FCSTD DOCUMENT  (FreeCAD 1.1R39747 (Git))
Label: FieldAssembly
License: All rights reserved
LicenseURL: https://en.wikipedia.org/wiki/All_rights_reserved
objects: App::Link×43, App::FeaturePython×43, App::Point×2, Assembly::JointGroup×2, Assembly::AssemblyLink×1, Assembly::AssemblyObject×1
EXTERNAL_REF file=RobotAssembly.FCStd obj=Assembly
EXTERNAL_REF file=RobotAssembly.FCStd obj=Body
EXTERNAL_REF file=RobotAssembly.FCStd obj=am_3637_NeveRest_Orbital_20_Gearmotor_REV2
EXTERNAL_REF file=RobotAssembly.FCStd obj=Motor_Mount_Right
EXTERNAL_REF file=RobotAssembly.FCStd obj=Motor_Mount_Left
EXTERNAL_REF file=RobotAssembly.FCStd obj=Link
EXTERNAL_REF file=RobotAssembly.FCStd obj=Slides_Mount
EXTERNAL_REF file=RobotAssembly.FCStd obj=Screw
EXTERNAL_REF file=RobotAssembly.FCStd obj=Screw001
EXTERNAL_REF file=RobotAssembly.FCStd obj=Screw002
EXTERNAL_REF file=RobotAssembly.FCStd obj=Screw003
EXTERNAL_REF file=RobotAssembly.FCStd obj=Screw004
EXTERNAL_REF file=RobotAssembly.FCStd obj=Screw005
EXTERNAL_REF file=RobotAssembly.FCStd obj=Screw006
EXTERNAL_REF file=RobotAssembly.FCStd obj=Screw007
EXTERNAL_REF file=RobotAssembly.FCStd obj=Link001
EXTERNAL_REF file=RobotAssembly.FCStd obj=Ras_Pi_3B_179
EXTERNAL_REF file=RobotAssembly.FCStd obj=Link002
EXTERNAL_REF file=RobotAssembly.FCStd obj=Screw008
EXTERNAL_REF file=RobotAssembly.FCStd obj=Link003
EXTERNAL_REF file=RobotAssembly.FCStd obj=Nut
EXTERNAL_REF file=RobotAssembly.FCStd obj=Body_Top
EXTERNAL_REF file=RobotAssembly.FCStd obj=Nut001
EXTERNAL_REF file=RobotAssembly.FCStd obj=Link004
EXTERNAL_REF file=RobotAssembly.FCStd obj=Link005
EXTERNAL_REF file=RobotAssembly.FCStd obj=Link007
EXTERNAL_REF file=RobotAssembly.FCStd obj=Link008
EXTERNAL_REF file=RobotAssembly.FCStd obj=Link009
EXTERNAL_REF file=RobotAssembly.FCStd obj=Link010
EXTERNAL_REF file=RobotAssembly.FCStd obj=Link011
EXTERNAL_REF file=RobotAssembly.FCStd obj=Link013
EXTERNAL_REF file=RobotAssembly.FCStd obj=Link012
EXTERNAL_REF file=RobotAssembly.FCStd obj=Link014
EXTERNAL_REF file=RobotAssembly.FCStd obj=Link015
EXTERNAL_REF file=RobotAssembly.FCStd obj=Link016
EXTERNAL_REF file=RobotAssembly.FCStd obj=Link017
EXTERNAL_REF file=RobotAssembly.FCStd obj=Link018
EXTERNAL_REF file=RobotAssembly.FCStd obj=SAR2_20_b
EXTERNAL_REF file=RobotAssembly.FCStd obj=SAR2_20_r
EXTERNAL_REF file=RobotAssembly.FCStd obj=_609_0613_0007
EXTERNAL_REF file=RobotAssembly.FCStd obj=StringGuard
EXTERNAL_REF file=RobotAssembly.FCStd obj=Screw009
EXTERNAL_REF file=RobotAssembly.FCStd obj=Link019
EXTERNAL_REF file=Field/Field.FCStd obj=Body

FEATURE [App::Point] Origin001
  Role = Origin
FEATURE [App::Point] Origin003
  Role = Origin
FEATURE [App::Link] Body
  LinkPlacement = pos=(-0.033439,2.054e-13,75.5) rot=(0,0,1;0rad)
  LinkedObject = -> <external RobotAssembly.FCStd>#Body
  Placement = pos=(-0.033439,2.054e-13,75.5) rot=(0,0,1;0rad)
FEATURE [App::Link] am_3637_NeveRest_Orbital_20_Gearmotor_REV2  label="am-3637 NeveRest Orbital 20 Gearmotor REV2"
  LinkPlacement = pos=(0.810701,-20.1819,58.942) rot=(1,0,0;1.5708rad)
  LinkedObject = -> <external RobotAssembly.FCStd>#am_3637_NeveRest_Orbital_20_Gearmotor_REV2
  Placement = pos=(0.810701,-20.1819,58.942) rot=(1,0,0;1.5708rad)
FEATURE [App::Link] Motor_Mount_Right  label="Motor Mount Right"
  LinkPlacement = pos=(-0.033439,2.089e-13,75.5) rot=(0,0,1;0rad)
  LinkedObject = -> <external RobotAssembly.FCStd>#Motor_Mount_Right
  Placement = pos=(-0.033439,2.089e-13,75.5) rot=(0,0,1;0rad)
FEATURE [App::Link] Motor_Mount_Left  label="Motor Mount Left"
  LinkPlacement = pos=(-85.0334,105,75.5) rot=(0,0,1;0rad)
  LinkedObject = -> <external RobotAssembly.FCStd>#Motor_Mount_Left
  Placement = pos=(-85.0334,105,75.5) rot=(0,0,1;0rad)
FEATURE [App::Link] Link  label="am-3637 NeveRest Orbital 20 Gearmotor REV003"
  LinkPlacement = pos=(-0.877579,20.1819,58.942) rot=(0,0.707107,0.707107;3.14159rad)
  LinkedObject = -> <external RobotAssembly.FCStd>#Link
  Placement = pos=(-0.877579,20.1819,58.942) rot=(0,0.707107,0.707107;3.14159rad)
FEATURE [App::Link] Slides_Mount  label="Slides Mount"
  LinkPlacement = pos=(-0.033439,1.861e-13,75.5) rot=(0,0,1;0rad)
  LinkedObject = -> <external RobotAssembly.FCStd>#Slides_Mount
  Placement = pos=(-0.033439,1.861e-13,75.5) rot=(0,0,1;0rad)
FEATURE [App::Link] Screw  label="M4x16-Screw053"
  LinkPlacement = pos=(79.9666,-25,105.5) rot=(0.57735,0.57735,0.57735;2.0944rad)
  LinkedObject = -> <external RobotAssembly.FCStd>#Screw
  Placement = pos=(79.9666,-25,105.5) rot=(0.57735,0.57735,0.57735;2.0944rad)
FEATURE [App::Link] Screw001  label="M4x16-Screw"
  LinkPlacement = pos=(79.9666,25,105.5) rot=(0.57735,0.57735,0.57735;2.0944rad)
  LinkedObject = -> <external RobotAssembly.FCStd>#Screw001
  Placement = pos=(79.9666,25,105.5) rot=(0.57735,0.57735,0.57735;2.0944rad)
FEATURE [App::Link] Screw002  label="M4x16-Screw054"
  LinkPlacement = pos=(79.9666,-25,80.5) rot=(0.57735,0.57735,0.57735;2.0944rad)
  LinkedObject = -> <external RobotAssembly.FCStd>#Screw002
  Placement = pos=(79.9666,-25,80.5) rot=(0.57735,0.57735,0.57735;2.0944rad)
FEATURE [App::Link] Screw003  label="M4x16-Screw055"
  LinkPlacement = pos=(79.9666,25,80.5) rot=(0.57735,0.57735,0.57735;2.0944rad)
  LinkedObject = -> <external RobotAssembly.FCStd>#Screw003
  Placement = pos=(79.9666,25,80.5) rot=(0.57735,0.57735,0.57735;2.0944rad)
FEATURE [App::Link] Screw004  label="M4x16-Screw056"
  LinkPlacement = pos=(-37.5334,-55,99.25) rot=(1,0,0;1.5708rad)
  LinkedObject = -> <external RobotAssembly.FCStd>#Screw004
  Placement = pos=(-37.5334,-55,99.25) rot=(1,0,0;1.5708rad)
FEATURE [App::Link] Screw005  label="M4x16-Screw057"
  LinkPlacement = pos=(-0.033439,-55,89.25) rot=(1,0,0;1.5708rad)
  LinkedObject = -> <external RobotAssembly.FCStd>#Screw005
  Placement = pos=(-0.033439,-55,89.25) rot=(1,0,0;1.5708rad)
FEATURE [App::Link] Screw006  label="M4x16-Screw058"
  LinkPlacement = pos=(-37.5334,-55,79.25) rot=(1,0,0;1.5708rad)
  LinkedObject = -> <external RobotAssembly.FCStd>#Screw006
  Placement = pos=(-37.5334,-55,79.25) rot=(1,0,0;1.5708rad)
FEATURE [App::Link] Screw007  label="M4x16-Screw059"
  LinkPlacement = pos=(37.4666,-55,79.25) rot=(1,0,0;1.5708rad)
  LinkedObject = -> <external RobotAssembly.FCStd>#Screw007
  Placement = pos=(37.4666,-55,79.25) rot=(1,0,0;1.5708rad)
FEATURE [App::Link] Link001  label="M4x16-Screw026"
  LinkPlacement = pos=(37.4666,-55,99.25) rot=(1,0,0;1.5708rad)
  LinkedObject = -> <external RobotAssembly.FCStd>#Link001
  Placement = pos=(37.4666,-55,99.25) rot=(1,0,0;1.5708rad)
FEATURE [App::Link] Ras_Pi_3B_179  label="Ras Pi 3B+179"
  LinkPlacement = pos=(19.4666,28,78.5) rot=(0,0.707107,0.707107;3.14159rad)
  LinkedObject = -> <external RobotAssembly.FCStd>#Ras_Pi_3B_179
  Placement = pos=(19.4666,28,78.5) rot=(0,0.707107,0.707107;3.14159rad)
FEATURE [App::Link] Link002  label="M4x14-Screw001"
  LinkPlacement = pos=(82.5201,-6.931e-13,138) rot=(0,1,0;1.5708rad)
  LinkedObject = -> <external RobotAssembly.FCStd>#Link002
  Placement = pos=(82.5201,-6.931e-13,138) rot=(0,1,0;1.5708rad)
FEATURE [App::Link] Screw008  label="M4x14-Screw"
  LinkPlacement = pos=(82.5201,-6.878e-13,223) rot=(0,1,0;1.5708rad)
  LinkedObject = -> <external RobotAssembly.FCStd>#Screw008
  Placement = pos=(82.5201,-6.878e-13,223) rot=(0,1,0;1.5708rad)
FEATURE [App::Link] Link003  label="M4-Nut001"
  LinkPlacement = pos=(71.7666,-6.97e-13,223) rot=(0.57735,0.57735,0.57735;2.0944rad)
  LinkedObject = -> <external RobotAssembly.FCStd>#Link003
  Placement = pos=(71.7666,-6.97e-13,223) rot=(0.57735,0.57735,0.57735;2.0944rad)
FEATURE [App::Link] Nut  label="M4-Nut"
  LinkPlacement = pos=(71.7666,-7.48e-13,138) rot=(0.57735,0.57735,0.57735;2.0944rad)
  LinkedObject = -> <external RobotAssembly.FCStd>#Nut
  Placement = pos=(71.7666,-7.48e-13,138) rot=(0.57735,0.57735,0.57735;2.0944rad)
FEATURE [App::Link] Body_Top  label="Body Top"
  LinkPlacement = pos=(-0.033439,2.036e-13,75.5) rot=(0,0,1;0rad)
  LinkedObject = -> <external RobotAssembly.FCStd>#Body_Top
  Placement = pos=(-0.033439,2.036e-13,75.5) rot=(0,0,1;0rad)
FEATURE [App::Link] Nut001  label="M4-Nut013"
  LinkPlacement = pos=(37.4666,-41.8,99.25) rot=(1,0,0;1.5708rad)
  LinkedObject = -> <external RobotAssembly.FCStd>#Nut001
  Placement = pos=(37.4666,-41.8,99.25) rot=(1,0,0;1.5708rad)
FEATURE [App::Link] Link004  label="M4-Nut003"
  LinkPlacement = pos=(-0.033439,-41.8,89.25) rot=(1,0,0;1.5708rad)
  LinkedObject = -> <external RobotAssembly.FCStd>#Link004
  Placement = pos=(-0.033439,-41.8,89.25) rot=(1,0,0;1.5708rad)
FEATURE [App::Link] Link005  label="M4-Nut004"
  LinkPlacement = pos=(-37.5334,-41.8,79.25) rot=(1,0,0;1.5708rad)
  LinkedObject = -> <external RobotAssembly.FCStd>#Link005
  Placement = pos=(-37.5334,-41.8,79.25) rot=(1,0,0;1.5708rad)
FEATURE [App::Link] Link007  label="M4-Nut006"
  LinkPlacement = pos=(-37.5334,-41.8,99.25) rot=(1,0,0;1.5708rad)
  LinkedObject = -> <external RobotAssembly.FCStd>#Link007
  Placement = pos=(-37.5334,-41.8,99.25) rot=(1,0,0;1.5708rad)
FEATURE [App::Link] Link008  label="M4-Nut007"
  LinkPlacement = pos=(-0.033439,41.8,89.25) rot=(1,0,0;4.71239rad)
  LinkedObject = -> <external RobotAssembly.FCStd>#Link008
  Placement = pos=(-0.033439,41.8,89.25) rot=(1,0,0;4.71239rad)
FEATURE [App::Link] Link009  label="M4-Nut008"
  LinkPlacement = pos=(-37.5334,41.8,99.25) rot=(1,0,0;4.71239rad)
  LinkedObject = -> <external RobotAssembly.FCStd>#Link009
  Placement = pos=(-37.5334,41.8,99.25) rot=(1,0,0;4.71239rad)
FEATURE [App::Link] Link010  label="M4-Nut009"
  LinkPlacement = pos=(-37.5334,41.8,79.25) rot=(1,0,0;4.71239rad)
  LinkedObject = -> <external RobotAssembly.FCStd>#Link010
  Placement = pos=(-37.5334,41.8,79.25) rot=(1,0,0;4.71239rad)
FEATURE [App::Link] Link011  label="M4-Nut010"
  LinkPlacement = pos=(37.4666,41.8,99.25) rot=(1,0,0;4.71239rad)
  LinkedObject = -> <external RobotAssembly.FCStd>#Link011
  Placement = pos=(37.4666,41.8,99.25) rot=(1,0,0;4.71239rad)
FEATURE [App::Link] Link013  label="M4-Nut012"
  LinkPlacement = pos=(37.4666,41.8,79.25) rot=(1,0,0;4.71239rad)
  LinkedObject = -> <external RobotAssembly.FCStd>#Link013
  Placement = pos=(37.4666,41.8,79.25) rot=(1,0,0;4.71239rad)
FEATURE [App::Link] Link012  label="M4-Nut011"
  LinkPlacement = pos=(37.4666,-41.8,79.25) rot=(1,0,0;1.5708rad)
  LinkedObject = -> <external RobotAssembly.FCStd>#Link012
  Placement = pos=(37.4666,-41.8,79.25) rot=(1,0,0;1.5708rad)
FEATURE [App::Link] Link014  label="M4x16-Screw034"
  LinkPlacement = pos=(-37.5334,55,99.25) rot=(0,0.707107,0.707107;3.14159rad)
  LinkedObject = -> <external RobotAssembly.FCStd>#Link014
  Placement = pos=(-37.5334,55,99.25) rot=(0,0.707107,0.707107;3.14159rad)
FEATURE [App::Link] Link015  label="M4x16-Screw035"
  LinkPlacement = pos=(37.4666,55,79.25) rot=(0,0.707107,0.707107;3.14159rad)
  LinkedObject = -> <external RobotAssembly.FCStd>#Link015
  Placement = pos=(37.4666,55,79.25) rot=(0,0.707107,0.707107;3.14159rad)
FEATURE [App::Link] Link016  label="M4x16-Screw036"
  LinkPlacement = pos=(-37.5334,55,79.25) rot=(0,0.707107,0.707107;3.14159rad)
  LinkedObject = -> <external RobotAssembly.FCStd>#Link016
  Placement = pos=(-37.5334,55,79.25) rot=(0,0.707107,0.707107;3.14159rad)
FEATURE [App::Link] Link017  label="M4x16-Screw037"
  LinkPlacement = pos=(37.4666,55,99.25) rot=(0,0.707107,0.707107;3.14159rad)
  LinkedObject = -> <external RobotAssembly.FCStd>#Link017
  Placement = pos=(37.4666,55,99.25) rot=(0,0.707107,0.707107;3.14159rad)
FEATURE [App::Link] Link018  label="M4x16-Screw038"
  LinkPlacement = pos=(-0.033439,55,89.25) rot=(0,0.707107,0.707107;3.14159rad)
  LinkedObject = -> <external RobotAssembly.FCStd>#Link018
  Placement = pos=(-0.033439,55,89.25) rot=(0,0.707107,0.707107;3.14159rad)
FEATURE [App::Link] SAR2_20_b  label="SAR2-20_b"
  LinkPlacement = pos=(87.3666,-10,38) rot=(0,0,1;0rad)
  LinkedObject = -> <external RobotAssembly.FCStd>#SAR2_20_b
  Placement = pos=(87.3666,-10,38) rot=(0,0,1;0rad)
FEATURE [App::Link] SAR2_20_r  label="SAR2-20_r"
  LinkPlacement = pos=(82.1666,-6.05,158) rot=(0,0,1;0rad)
  LinkedObject = -> <external RobotAssembly.FCStd>#SAR2_20_r
  Placement = pos=(82.1666,-6.05,158) rot=(0,0,1;0rad)
FEATURE [App::Link] _609_0613_0007  label="1609-0613-0007"
  LinkPlacement = pos=(64.9666,18.5,220) rot=(0,1,0;1.57081rad)
  LinkedObject = -> <external RobotAssembly.FCStd>#_609_0613_0007
  Placement = pos=(64.9666,18.5,220) rot=(0,1,0;1.57081rad)
FEATURE [App::Link] StringGuard
  LinkPlacement = pos=(64.9666,18.25,220) rot=(0,0,1;0rad)
  LinkedObject = -> <external RobotAssembly.FCStd>#StringGuard
  Placement = pos=(64.9666,18.25,220) rot=(0,0,1;0rad)
FEATURE [App::Link] Screw009  label="M4x25-Screw"
  LinkPlacement = pos=(64.9666,27.5,220) rot=(1,0,0;4.71239rad)
  LinkedObject = -> <external RobotAssembly.FCStd>#Screw009
  Placement = pos=(64.9666,27.5,220) rot=(1,0,0;4.71239rad)
FEATURE [App::Link] Link019  label="M4-Nut014"
  LinkPlacement = pos=(64.9666,10,220) rot=(0,-0.707107,0.707107;3.14159rad)
  LinkedObject = -> <external RobotAssembly.FCStd>#Link019
  Placement = pos=(64.9666,10,220) rot=(0,-0.707107,0.707107;3.14159rad)
FEATURE [App::Link] Field
  LinkedObject = -> <external Field/Field.FCStd>#Body
FEATURE [App::FeaturePython] GroundedJoint  # Assembly grounded joint (typed FeaturePython)
  ObjectToGround = -> Field
FEATURE [App::FeaturePython] Joint  label="Distance"  # Assembly joint (typed FeaturePython)
  Activated = true
  AngleMax = 0
  AngleMin = 0
  Detach1 = false
  Detach2 = false
  Distance = -50
  Distance2 = 0
  EnableAngleMax = false
  EnableAngleMin = false
  EnableLengthMax = false
  EnableLengthMin = false
  JointType = 5 (Distance)
  LengthMax = 0
  LengthMin = 0
  Placement1 = pos=(0.033439,-1.12e-13,-7.5) rot=(0,0,1;0rad)
  Placement2 = pos=(-1.386e-13,1.101e-13,18) rot=(0,0,1;0rad)
  Reference1 = -> Assembly [Robot_Assembly.Body.Face26,Robot_Assembly.Body.Vertex125]
  Reference2 = -> Assembly [Field.Face5,Field.Vertex11]
FEATURE [Assembly::JointGroup] Joints
  Group = -> [GroundedJoint,Joint]
FEATURE [App::FeaturePython] Joint002  label="Fixed"  # Assembly joint (typed FeaturePython)
  Activated = true
  AngleMax = 0
  AngleMin = 0
  Detach1 = false
  Detach2 = false
  Distance = 0
  Distance2 = 0
  EnableAngleMax = false
  EnableAngleMin = false
  EnableLengthMax = false
  EnableLengthMin = false
  JointType = 0 (Fixed)
  LengthMax = 0
  LengthMin = 0
  Placement1 = pos=(0,-50,13.75) rot=(1,0,0;1.5708rad)
  Placement2 = pos=(0,-50,13.75) rot=(1,0,0;1.5708rad)
  Reference1 = -> Assembly [Robot_Assembly.Motor_Mount_Right.Edge47,Robot_Assembly.Motor_Mount_Right.Edge47]
  Reference2 = -> Assembly [Robot_Assembly.Body.Edge30,Robot_Assembly.Body.Edge30]
FEATURE [App::FeaturePython] Joint003  label="Fixed001"  # Assembly joint (typed FeaturePython)
  Activated = true
  AngleMax = 0
  AngleMin = 0
  Detach1 = false
  Detach2 = false
  Distance = 0
  Distance2 = 0
  EnableAngleMax = false
  EnableAngleMin = false
  EnableLengthMax = false
  EnableLengthMin = false
  JointType = 0 (Fixed)
  LengthMax = 0
  LengthMin = 0
  Offset2 = pos=(0,0,0) rot=(0,0,1;3.14159rad)
  Placement1 = pos=(85,-55,13.75) rot=(0,0.707107,0.707107;3.14159rad)
  Placement2 = pos=(0,50,13.75) rot=(0,-0.707107,0.707107;3.14159rad)
  Reference1 = -> Assembly [Robot_Assembly.Motor_Mount_Left.Edge48,Robot_Assembly.Motor_Mount_Left.Edge48]
  Reference2 = -> Assembly [Robot_Assembly.Body.Edge59,Robot_Assembly.Body.Edge59]
FEATURE [App::FeaturePython] Joint004  label="Fixed002"  # Assembly joint (typed FeaturePython)
  Activated = true
  AngleMax = 0
  AngleMin = 0
  Detach1 = false
  Detach2 = false
  Distance = 0
  Distance2 = 0
  EnableAngleMax = false
  EnableAngleMin = false
  EnableLengthMax = false
  EnableLengthMin = false
  JointType = 0 (Fixed)
  LengthMax = 0
  LengthMin = 0
  Placement1 = pos=(0,0,32.1564) rot=(0,0,1;0rad)
  Placement2 = pos=(-28,-50,-29) rot=(1,0,0;1.5708rad)
  Reference1 = -> <external RobotAssembly.FCStd>#Assembly [am_3637_NeveRest_Orbital_20_Gearmotor_REV2.Part__Feature.Edge163,am_3637_NeveRest_Orbital_20_Gearmotor_REV2.Part__Feature.Edge163]
  Reference2 = -> Assembly [Robot_Assembly.Motor_Mount_Right.Edge38,Robot_Assembly.Motor_Mount_Right.Edge38]
FEATURE [App::FeaturePython] Joint005  label="Fixed003"  # Assembly joint (typed FeaturePython)
  Activated = true
  AngleMax = 0
  AngleMin = 0
  Detach1 = false
  Detach2 = false
  Distance = 0
  Distance2 = 0
  EnableAngleMax = false
  EnableAngleMin = false
  EnableLengthMax = false
  EnableLengthMin = false
  JointType = 0 (Fixed)
  LengthMax = 0
  LengthMin = 0
  Placement1 = pos=(0,0,32.1564) rot=(0,0,1;0rad)
  Placement2 = pos=(113,-55,-29) rot=(0,0.707107,0.707107;3.14159rad)
  Reference1 = -> <external RobotAssembly.FCStd>#Assembly [Link.Part__Feature.Edge163,Link.Part__Feature.Edge163]
  Reference2 = -> Assembly [Robot_Assembly.Motor_Mount_Left.Edge39,Robot_Assembly.Motor_Mount_Left.Edge39]
FEATURE [App::FeaturePython] Joint009  label="Fixed005"  # Assembly joint (typed FeaturePython)
  Activated = true
  AngleMax = 0
  AngleMin = 0
  Detach1 = false
  Detach2 = false
  Distance = 0
  Distance2 = 0
  EnableAngleMax = false
  EnableAngleMin = false
  EnableLengthMax = false
  EnableLengthMin = false
  JointType = 0 (Fixed)
  LengthMax = 0
  LengthMin = 0
  Placement1 = pos=(75,25,30) rot=(0.57735,0.57735,0.57735;2.0944rad)
  Placement2 = pos=(75,25,30) rot=(0.57735,0.57735,0.57735;2.0944rad)
  Reference1 = -> Assembly [Robot_Assembly.Slides_Mount.Edge60,Robot_Assembly.Slides_Mount.Edge60]
  Reference2 = -> Assembly [Robot_Assembly.Body.Edge44,Robot_Assembly.Body.Edge44]
FEATURE [App::FeaturePython] Joint012  label="Fixed007"  # Assembly joint (typed FeaturePython)
  Activated = true
  AngleMax = 0
  AngleMin = 0
  Detach1 = false
  Detach2 = false
  Distance = 0
  Distance2 = 0
  EnableAngleMax = false
  EnableAngleMin = false
  EnableLengthMax = false
  EnableLengthMin = false
  JointType = 0 (Fixed)
  LengthMax = 0
  LengthMin = 0
  Placement2 = pos=(80,-25,30) rot=(0.57735,0.57735,0.57735;2.0944rad)
  Reference1 = -> Assembly [Robot_Assembly.Screw.Edge26,Robot_Assembly.Screw.Edge26]
  Reference2 = -> Assembly [Robot_Assembly.Slides_Mount.Edge74,Robot_Assembly.Slides_Mount.Edge74]
FEATURE [App::FeaturePython] Joint013  label="Fixed008"  # Assembly joint (typed FeaturePython)
  Activated = true
  AngleMax = 0
  AngleMin = 0
  Detach1 = false
  Detach2 = false
  Distance = 0
  Distance2 = 0
  EnableAngleMax = false
  EnableAngleMin = false
  EnableLengthMax = false
  EnableLengthMin = false
  JointType = 0 (Fixed)
  LengthMax = 0
  LengthMin = 0
  Placement2 = pos=(80,-25,5) rot=(0.57735,0.57735,0.57735;2.0944rad)
  Reference1 = -> Assembly [Robot_Assembly.Screw002.Edge26,Robot_Assembly.Screw002.Edge26]
  Reference2 = -> Assembly [Robot_Assembly.Slides_Mount.Edge72,Robot_Assembly.Slides_Mount.Edge72]
FEATURE [App::FeaturePython] Joint014  label="Fixed009"  # Assembly joint (typed FeaturePython)
  Activated = true
  AngleMax = 0
  AngleMin = 0
  Detach1 = false
  Detach2 = false
  Distance = 0
  Distance2 = 0
  EnableAngleMax = false
  EnableAngleMin = false
  EnableLengthMax = false
  EnableLengthMin = false
  JointType = 0 (Fixed)
  LengthMax = 0
  LengthMin = 0
  Placement2 = pos=(80,25,30) rot=(0.57735,0.57735,0.57735;2.0944rad)
  Reference1 = -> Assembly [Robot_Assembly.Screw001.Edge26,Robot_Assembly.Screw001.Edge26]
  Reference2 = -> Assembly [Robot_Assembly.Slides_Mount.Edge70,Robot_Assembly.Slides_Mount.Edge70]
FEATURE [App::FeaturePython] Joint015  label="Fixed010"  # Assembly joint (typed FeaturePython)
  Activated = true
  AngleMax = 0
  AngleMin = 0
  Detach1 = false
  Detach2 = false
  Distance = 0
  Distance2 = 0
  EnableAngleMax = false
  EnableAngleMin = false
  EnableLengthMax = false
  EnableLengthMin = false
  JointType = 0 (Fixed)
  LengthMax = 0
  LengthMin = 0
  Placement2 = pos=(80,25,5) rot=(0.57735,0.57735,0.57735;2.0944rad)
  Reference1 = -> Assembly [Robot_Assembly.Screw003.Edge26,Robot_Assembly.Screw003.Edge26]
  Reference2 = -> Assembly [Robot_Assembly.Slides_Mount.Edge68,Robot_Assembly.Slides_Mount.Edge68]
FEATURE [App::FeaturePython] Joint016  label="Fixed011"  # Assembly joint (typed FeaturePython)
  Activated = true
  AngleMax = 0
  AngleMin = 0
  Detach1 = false
  Detach2 = false
  Distance = 0
  Distance2 = 0
  EnableAngleMax = false
  EnableAngleMin = false
  EnableLengthMax = false
  EnableLengthMin = false
  JointType = 0 (Fixed)
  LengthMax = 0
  LengthMin = 0
  Placement2 = pos=(-37.5,-55,23.75) rot=(1,0,0;1.5708rad)
  Reference1 = -> Assembly [Robot_Assembly.Screw004.Edge26,Robot_Assembly.Screw004.Edge26]
  Reference2 = -> Assembly [Robot_Assembly.Motor_Mount_Right.Edge45,Robot_Assembly.Motor_Mount_Right.Edge45]
FEATURE [App::FeaturePython] Joint017  label="Fixed012"  # Assembly joint (typed FeaturePython)
  Activated = true
  AngleMax = 0
  AngleMin = 0
  Detach1 = false
  Detach2 = false
  Distance = 0
  Distance2 = 0
  EnableAngleMax = false
  EnableAngleMin = false
  EnableLengthMax = false
  EnableLengthMin = false
  JointType = 0 (Fixed)
  LengthMax = 0
  LengthMin = 0
  Placement2 = pos=(-37.5,-55,3.75) rot=(1,0,0;1.5708rad)
  Reference1 = -> Assembly [Robot_Assembly.Screw006.Edge26,Robot_Assembly.Screw006.Edge26]
  Reference2 = -> Assembly [Robot_Assembly.Motor_Mount_Right.Edge54,Robot_Assembly.Motor_Mount_Right.Edge54]
FEATURE [App::FeaturePython] Joint018  label="Fixed013"  # Assembly joint (typed FeaturePython)
  Activated = true
  AngleMax = 0
  AngleMin = 0
  Detach1 = false
  Detach2 = false
  Distance = 0
  Distance2 = 0
  EnableAngleMax = false
  EnableAngleMin = false
  EnableLengthMax = false
  EnableLengthMin = false
  JointType = 0 (Fixed)
  LengthMax = 0
  LengthMin = 0
  Placement2 = pos=(0,-55,13.75) rot=(1,0,0;1.5708rad)
  Reference1 = -> Assembly [Robot_Assembly.Screw005.Edge26,Robot_Assembly.Screw005.Edge26]
  Reference2 = -> Assembly [Robot_Assembly.Motor_Mount_Right.Edge48,Robot_Assembly.Motor_Mount_Right.Edge48]
FEATURE [App::FeaturePython] Joint019  label="Fixed014"  # Assembly joint (typed FeaturePython)
  Activated = true
  AngleMax = 0
  AngleMin = 0
  Detach1 = false
  Detach2 = false
  Distance = 0
  Distance2 = 0
  EnableAngleMax = false
  EnableAngleMin = false
  EnableLengthMax = false
  EnableLengthMin = false
  JointType = 0 (Fixed)
  LengthMax = 0
  LengthMin = 0
  Placement2 = pos=(37.5,-55,3.75) rot=(1,0,0;1.5708rad)
  Reference1 = -> Assembly [Robot_Assembly.Screw007.Edge26,Robot_Assembly.Screw007.Edge26]
  Reference2 = -> Assembly [Robot_Assembly.Motor_Mount_Right.Edge51,Robot_Assembly.Motor_Mount_Right.Edge51]
FEATURE [App::FeaturePython] Joint020  label="Fixed015"  # Assembly joint (typed FeaturePython)
  Activated = true
  AngleMax = 0
  AngleMin = 0
  Detach1 = false
  Detach2 = false
  Distance = 0
  Distance2 = 0
  EnableAngleMax = false
  EnableAngleMin = false
  EnableLengthMax = false
  EnableLengthMin = false
  JointType = 0 (Fixed)
  LengthMax = 0
  LengthMin = 0
  Placement2 = pos=(37.5,-55,23.75) rot=(1,0,0;1.5708rad)
  Reference1 = -> Assembly [Robot_Assembly.Link001.Edge26,Robot_Assembly.Link001.Edge26]
  Reference2 = -> Assembly [Robot_Assembly.Motor_Mount_Right.Edge42,Robot_Assembly.Motor_Mount_Right.Edge42]
FEATURE [App::FeaturePython] Joint023  label="Fixed017"  # Assembly joint (typed FeaturePython)
  Activated = true
  AngleMax = 0
  AngleMin = 0
  Detach1 = false
  Detach2 = false
  Distance = 0
  Distance2 = 0
  EnableAngleMax = false
  EnableAngleMin = false
  EnableLengthMax = false
  EnableLengthMin = false
  JointType = 0 (Fixed)
  LengthMax = 0
  LengthMin = 0
  Placement1 = pos=(0,0,3.2) rot=(0,0,1;0rad)
  Placement2 = pos=(75,-1.0119e-12,62.5) rot=(0.57735,0.57735,0.57735;2.0944rad)
  Reference1 = -> Assembly [Robot_Assembly.Nut.Edge2,Robot_Assembly.Nut.Edge2]
  Reference2 = -> Assembly [Robot_Assembly.Slides_Mount.Edge58,Robot_Assembly.Slides_Mount.Edge58]
FEATURE [App::FeaturePython] Joint024  label="Fixed018"  # Assembly joint (typed FeaturePython)
  Activated = true
  AngleMax = 0
  AngleMin = 0
  Detach1 = false
  Detach2 = false
  Distance = 0
  Distance2 = 0
  EnableAngleMax = false
  EnableAngleMin = false
  EnableLengthMax = false
  EnableLengthMin = false
  JointType = 0 (Fixed)
  LengthMax = 0
  LengthMin = 0
  Placement1 = pos=(0,0,3.2) rot=(0,0,1;0rad)
  Placement2 = pos=(75,-9.797e-13,147.5) rot=(0.57735,0.57735,0.57735;2.0944rad)
  Reference1 = -> Assembly [Robot_Assembly.Link003.Edge2,Robot_Assembly.Link003.Edge2]
  Reference2 = -> Assembly [Robot_Assembly.Slides_Mount.Edge57,Robot_Assembly.Slides_Mount.Edge57]
FEATURE [App::FeaturePython] Joint027  label="Fixed021"  # Assembly joint (typed FeaturePython)
  Activated = true
  AngleMax = 0
  AngleMin = 0
  Detach1 = false
  Detach2 = false
  Distance = 0
  Distance2 = 0
  EnableAngleMax = false
  EnableAngleMin = false
  EnableLengthMax = false
  EnableLengthMin = false
  JointType = 0 (Fixed)
  LengthMax = 0
  LengthMin = 0
  Offset2 = pos=(0,0,0) rot=(0,0,1;1.5708rad)
  Placement1 = pos=(-42,-24.5,3) rot=(0,0,1;0rad)
  Placement2 = pos=(61.5,0,-52.5) rot=(0,0.707107,0.707107;3.14159rad)
  Reference1 = -> Assembly [Robot_Assembly.Body.Edge196,Robot_Assembly.Body.Edge196]
  Reference2 = -> <external RobotAssembly.FCStd>#Assembly [Ras_Pi_3B_179.Part__Feature014.Edge10,Ras_Pi_3B_179.Part__Feature014.Edge10]
FEATURE [App::FeaturePython] Joint028  label="Fixed022"  # Assembly joint (typed FeaturePython)
  Activated = true
  AngleMax = 0
  AngleMin = 0
  Detach1 = false
  Detach2 = false
  Distance = 0
  Distance2 = 0
  EnableAngleMax = false
  EnableAngleMin = false
  EnableLengthMax = false
  EnableLengthMin = false
  JointType = 0 (Fixed)
  LengthMax = 0
  LengthMin = 0
  Placement1 = pos=(-66,-41,35) rot=(0,0,1;0rad)
  Placement2 = pos=(-66,-41,35) rot=(0,0,1;0rad)
  Reference1 = -> Assembly [Robot_Assembly.Body.Edge24,Robot_Assembly.Body.Edge24]
  Reference2 = -> Assembly [Robot_Assembly.Body_Top.Edge47,Robot_Assembly.Body_Top.Edge47]
FEATURE [App::FeaturePython] Joint029  label="Fixed023"  # Assembly joint (typed FeaturePython)
  Activated = true
  AngleMax = 0
  AngleMin = 0
  Detach1 = false
  Detach2 = false
  Distance = 0
  Distance2 = 0
  EnableAngleMax = false
  EnableAngleMin = false
  EnableLengthMax = false
  EnableLengthMin = false
  JointType = 0 (Fixed)
  LengthMax = 0
  LengthMin = 0
  Placement1 = pos=(-7.1e-15,0,3.2) rot=(0,0,1;0rad)
  Placement2 = pos=(37.5,-45,23.75) rot=(1,0,0;1.5708rad)
  Reference1 = -> Assembly [Robot_Assembly.Nut001.Edge2,Robot_Assembly.Nut001.Edge2]
  Reference2 = -> Assembly [Robot_Assembly.Body.Edge93,Robot_Assembly.Body.Edge93]
FEATURE [App::FeaturePython] Joint030  label="Fixed024"  # Assembly joint (typed FeaturePython)
  Activated = true
  AngleMax = 0
  AngleMin = 0
  Detach1 = false
  Detach2 = false
  Distance = 0
  Distance2 = 0
  EnableAngleMax = false
  EnableAngleMin = false
  EnableLengthMax = false
  EnableLengthMin = false
  JointType = 0 (Fixed)
  LengthMax = 0
  LengthMin = 0
  Placement1 = pos=(0,0,3.2) rot=(0,0,1;0rad)
  Placement2 = pos=(0,-45,13.75) rot=(1,0,0;1.5708rad)
  Reference1 = -> Assembly [Robot_Assembly.Link004.Edge2,Robot_Assembly.Link004.Edge2]
  Reference2 = -> Assembly [Robot_Assembly.Body.Edge102,Robot_Assembly.Body.Edge102]
FEATURE [App::FeaturePython] Joint031  label="Fixed025"  # Assembly joint (typed FeaturePython)
  Activated = true
  AngleMax = 0
  AngleMin = 0
  Detach1 = false
  Detach2 = false
  Distance = 0
  Distance2 = 0
  EnableAngleMax = false
  EnableAngleMin = false
  EnableLengthMax = false
  EnableLengthMin = false
  JointType = 0 (Fixed)
  LengthMax = 0
  LengthMin = 0
  Placement1 = pos=(-7.1e-15,0,3.2) rot=(0,0,1;0rad)
  Placement2 = pos=(-37.5,-45,23.75) rot=(1,0,0;1.5708rad)
  Reference1 = -> Assembly [Robot_Assembly.Link007.Edge2,Robot_Assembly.Link007.Edge2]
  Reference2 = -> Assembly [Robot_Assembly.Body.Edge92,Robot_Assembly.Body.Edge92]
FEATURE [App::FeaturePython] Joint032  label="Fixed026"  # Assembly joint (typed FeaturePython)
  Activated = true
  AngleMax = 0
  AngleMin = 0
  Detach1 = false
  Detach2 = false
  Distance = 0
  Distance2 = 0
  EnableAngleMax = false
  EnableAngleMin = false
  EnableLengthMax = false
  EnableLengthMin = false
  JointType = 0 (Fixed)
  LengthMax = 0
  LengthMin = 0
  Placement1 = pos=(-7.1e-15,0,3.2) rot=(0,0,1;0rad)
  Placement2 = pos=(-37.5,-45,3.75) rot=(1,0,0;1.5708rad)
  Reference1 = -> Assembly [Robot_Assembly.Link005.Edge2,Robot_Assembly.Link005.Edge2]
  Reference2 = -> Assembly [Robot_Assembly.Body.Edge103,Robot_Assembly.Body.Edge103]
FEATURE [App::FeaturePython] Joint033  label="Fixed027"  # Assembly joint (typed FeaturePython)
  Activated = true
  AngleMax = 0
  AngleMin = 0
  Detach1 = false
  Detach2 = false
  Distance = 0
  Distance2 = 0
  EnableAngleMax = false
  EnableAngleMin = false
  EnableLengthMax = false
  EnableLengthMin = false
  JointType = 0 (Fixed)
  LengthMax = 0
  LengthMin = 0
  Placement1 = pos=(0,0,3.2) rot=(0,0,1;0rad)
  Placement2 = pos=(0,45,13.75) rot=(1,0,0;1.5708rad)
  Reference1 = -> Assembly [Robot_Assembly.Link008.Edge2,Robot_Assembly.Link008.Edge2]
  Reference2 = -> Assembly [Robot_Assembly.Body.Edge135,Robot_Assembly.Body.Edge135]
FEATURE [App::FeaturePython] Joint034  label="Fixed028"  # Assembly joint (typed FeaturePython)
  Activated = true
  AngleMax = 0
  AngleMin = 0
  Detach1 = false
  Detach2 = false
  Distance = 0
  Distance2 = 0
  EnableAngleMax = false
  EnableAngleMin = false
  EnableLengthMax = false
  EnableLengthMin = false
  JointType = 0 (Fixed)
  LengthMax = 0
  LengthMin = 0
  Placement1 = pos=(7.1e-15,0,3.2) rot=(0,0,1;0rad)
  Placement2 = pos=(-37.5,45,23.75) rot=(1,0,0;1.5708rad)
  Reference1 = -> Assembly [Robot_Assembly.Link009.Edge2,Robot_Assembly.Link009.Edge2]
  Reference2 = -> Assembly [Robot_Assembly.Body.Edge126,Robot_Assembly.Body.Edge126]
FEATURE [App::FeaturePython] Joint035  label="Fixed029"  # Assembly joint (typed FeaturePython)
  Activated = true
  AngleMax = 0
  AngleMin = 0
  Detach1 = false
  Detach2 = false
  Distance = 0
  Distance2 = 0
  EnableAngleMax = false
  EnableAngleMin = false
  EnableLengthMax = false
  EnableLengthMin = false
  JointType = 0 (Fixed)
  LengthMax = 0
  LengthMin = 0
  Placement1 = pos=(7.1e-15,0,3.2) rot=(0,0,1;0rad)
  Placement2 = pos=(-37.5,45,3.75) rot=(1,0,0;1.5708rad)
  Reference1 = -> Assembly [Robot_Assembly.Link010.Edge2,Robot_Assembly.Link010.Edge2]
  Reference2 = -> Assembly [Robot_Assembly.Body.Edge137,Robot_Assembly.Body.Edge137]
FEATURE [App::FeaturePython] Joint036  label="Fixed030"  # Assembly joint (typed FeaturePython)
  Activated = true
  AngleMax = 0
  AngleMin = 0
  Detach1 = false
  Detach2 = false
  Distance = 0
  Distance2 = 0
  EnableAngleMax = false
  EnableAngleMin = false
  EnableLengthMax = false
  EnableLengthMin = false
  JointType = 0 (Fixed)
  LengthMax = 0
  LengthMin = 0
  Placement1 = pos=(7.1e-15,0,3.2) rot=(0,0,1;0rad)
  Placement2 = pos=(37.5,45,3.75) rot=(1,0,0;1.5708rad)
  Reference1 = -> Assembly [Robot_Assembly.Link013.Edge2,Robot_Assembly.Link013.Edge2]
  Reference2 = -> Assembly [Robot_Assembly.Body.Edge136,Robot_Assembly.Body.Edge136]
FEATURE [App::FeaturePython] Joint037  label="Fixed031"  # Assembly joint (typed FeaturePython)
  Activated = true
  AngleMax = 0
  AngleMin = 0
  Detach1 = false
  Detach2 = false
  Distance = 0
  Distance2 = 0
  EnableAngleMax = false
  EnableAngleMin = false
  EnableLengthMax = false
  EnableLengthMin = false
  JointType = 0 (Fixed)
  LengthMax = 0
  LengthMin = 0
  Placement1 = pos=(7.1e-15,0,3.2) rot=(0,0,1;0rad)
  Placement2 = pos=(37.5,45,23.75) rot=(1,0,0;1.5708rad)
  Reference1 = -> Assembly [Robot_Assembly.Link011.Edge2,Robot_Assembly.Link011.Edge2]
  Reference2 = -> Assembly [Robot_Assembly.Body.Edge125,Robot_Assembly.Body.Edge125]
FEATURE [App::FeaturePython] Joint038  label="Fixed032"  # Assembly joint (typed FeaturePython)
  Activated = true
  AngleMax = 0
  AngleMin = 0
  Detach1 = false
  Detach2 = false
  Distance = 0
  Distance2 = 0
  EnableAngleMax = false
  EnableAngleMin = false
  EnableLengthMax = false
  EnableLengthMin = false
  JointType = 0 (Fixed)
  LengthMax = 0
  LengthMin = 0
  Placement1 = pos=(-7.1e-15,0,3.2) rot=(0,0,1;0rad)
  Placement2 = pos=(37.5,-45,3.75) rot=(1,0,0;1.5708rad)
  Reference1 = -> Assembly [Robot_Assembly.Link012.Edge2,Robot_Assembly.Link012.Edge2]
  Reference2 = -> Assembly [Robot_Assembly.Body.Edge104,Robot_Assembly.Body.Edge104]
FEATURE [App::FeaturePython] Joint039  label="Fixed033"  # Assembly joint (typed FeaturePython)
  Activated = true
  AngleMax = 0
  AngleMin = 0
  Detach1 = false
  Detach2 = false
  Distance = 0
  Distance2 = 0
  EnableAngleMax = false
  EnableAngleMin = false
  EnableLengthMax = false
  EnableLengthMin = false
  JointType = 0 (Fixed)
  LengthMax = 0
  LengthMin = 0
  Placement2 = pos=(47.5,-50,23.75) rot=(0,0.707107,0.707107;3.14159rad)
  Reference1 = -> Assembly [Robot_Assembly.Link014.Edge26,Robot_Assembly.Link014.Edge26]
  Reference2 = -> Assembly [Robot_Assembly.Motor_Mount_Left.Edge41,Robot_Assembly.Motor_Mount_Left.Edge41]
FEATURE [App::FeaturePython] Joint040  label="Fixed034"  # Assembly joint (typed FeaturePython)
  Activated = true
  AngleMax = 0
  AngleMin = 0
  Detach1 = false
  Detach2 = false
  Distance = 0
  Distance2 = 0
  EnableAngleMax = false
  EnableAngleMin = false
  EnableLengthMax = false
  EnableLengthMin = false
  JointType = 0 (Fixed)
  LengthMax = 0
  LengthMin = 0
  Placement2 = pos=(122.5,-50,3.75) rot=(0,0.707107,0.707107;3.14159rad)
  Reference1 = -> Assembly [Robot_Assembly.Link015.Edge26,Robot_Assembly.Link015.Edge26]
  Reference2 = -> Assembly [Robot_Assembly.Motor_Mount_Left.Edge53,Robot_Assembly.Motor_Mount_Left.Edge53]
FEATURE [App::FeaturePython] Joint041  label="Fixed035"  # Assembly joint (typed FeaturePython)
  Activated = true
  AngleMax = 0
  AngleMin = 0
  Detach1 = false
  Detach2 = false
  Distance = 0
  Distance2 = 0
  EnableAngleMax = false
  EnableAngleMin = false
  EnableLengthMax = false
  EnableLengthMin = false
  JointType = 0 (Fixed)
  LengthMax = 0
  LengthMin = 0
  Placement2 = pos=(85,-50,13.75) rot=(0,0.707107,0.707107;3.14159rad)
  Reference1 = -> Assembly [Robot_Assembly.Link018.Edge26,Robot_Assembly.Link018.Edge26]
  Reference2 = -> Assembly [Robot_Assembly.Motor_Mount_Left.Edge47,Robot_Assembly.Motor_Mount_Left.Edge47]
FEATURE [App::FeaturePython] Joint042  label="Fixed036"  # Assembly joint (typed FeaturePython)
  Activated = true
  AngleMax = 0
  AngleMin = 0
  Detach1 = false
  Detach2 = false
  Distance = 0
  Distance2 = 0
  EnableAngleMax = false
  EnableAngleMin = false
  EnableLengthMax = false
  EnableLengthMin = false
  JointType = 0 (Fixed)
  LengthMax = 0
  LengthMin = 0
  Placement2 = pos=(47.5,-50,3.75) rot=(0,0.707107,0.707107;3.14159rad)
  Reference1 = -> Assembly [Robot_Assembly.Link016.Edge26,Robot_Assembly.Link016.Edge26]
  Reference2 = -> Assembly [Robot_Assembly.Motor_Mount_Left.Edge50,Robot_Assembly.Motor_Mount_Left.Edge50]
FEATURE [App::FeaturePython] Joint043  label="Fixed037"  # Assembly joint (typed FeaturePython)
  Activated = true
  AngleMax = 0
  AngleMin = 0
  Detach1 = false
  Detach2 = false
  Distance = 0
  Distance2 = 0
  EnableAngleMax = false
  EnableAngleMin = false
  EnableLengthMax = false
  EnableLengthMin = false
  JointType = 0 (Fixed)
  LengthMax = 0
  LengthMin = 0
  Placement2 = pos=(122.5,-50,23.75) rot=(0,0.707107,0.707107;3.14159rad)
  Reference1 = -> Assembly [Robot_Assembly.Link017.Edge26,Robot_Assembly.Link017.Edge26]
  Reference2 = -> Assembly [Robot_Assembly.Motor_Mount_Left.Edge44,Robot_Assembly.Motor_Mount_Left.Edge44]
FEATURE [App::FeaturePython] Joint044  label="Slider"  # Assembly joint (typed FeaturePython)
  Activated = true
  AngleMax = 0
  AngleMin = 0
  Detach1 = false
  Detach2 = false
  Distance = 0
  Distance2 = 0
  EnableAngleMax = false
  EnableAngleMin = false
  EnableLengthMax = true
  EnableLengthMin = true
  JointType = 3 (Slider)
  LengthMax = 0
  LengthMin = -120
  Offset1 = pos=(-2.9952,0,0) rot=(0,0,1;0rad)
  Placement1 = pos=(0.302211,6.05,200) rot=(0,0,1;0rad)
  Placement2 = pos=(-4.89776,10,200) rot=(0,0,1;0rad)
  Reference1 = -> Assembly [Robot_Assembly.SAR2_20_r.Face24,Robot_Assembly.SAR2_20_r.Face24]
  Reference2 = -> Assembly [Robot_Assembly.SAR2_20_b.Face57,Robot_Assembly.SAR2_20_b.Face57]
FEATURE [App::FeaturePython] Joint045  label="Fixed038"  # Assembly joint (typed FeaturePython)
  Activated = true
  AngleMax = 0
  AngleMin = 0
  Detach1 = false
  Detach2 = false
  Distance = 0
  Distance2 = 0
  EnableAngleMax = false
  EnableAngleMin = false
  EnableLengthMax = false
  EnableLengthMin = false
  JointType = 0 (Fixed)
  LengthMax = 0
  LengthMin = 0
  Offset2 = pos=(0,0,0) rot=(0,0,-1;1.5708rad)
  Placement1 = pos=(-7.4,10,185) rot=(0,1,0;1.5708rad)
  Placement2 = pos=(80,-9.797e-13,147.5) rot=(0,1,0;1.5708rad)
  Reference1 = -> Assembly [Robot_Assembly.SAR2_20_b.Edge129,Robot_Assembly.SAR2_20_b.Edge129]
  Reference2 = -> Assembly [Robot_Assembly.Slides_Mount.Edge64,Robot_Assembly.Slides_Mount.Edge64]
FEATURE [App::FeaturePython] Joint046  label="Fixed039"  # Assembly joint (typed FeaturePython)
  Activated = true
  AngleMax = 0
  AngleMin = 0
  Detach1 = false
  Detach2 = false
  Distance = 0
  Distance2 = 0
  EnableAngleMax = false
  EnableAngleMin = false
  EnableLengthMax = false
  EnableLengthMin = false
  JointType = 0 (Fixed)
  LengthMax = 0
  LengthMin = 0
  Placement1 = pos=(0,0,-2.55355) rot=(0,0,1;0rad)
  Placement2 = pos=(-7.4,10,185) rot=(0,1,0;1.5708rad)
  Reference1 = -> Assembly [Robot_Assembly.Screw008.Edge4,Robot_Assembly.Screw008.Edge4]
  Reference2 = -> Assembly [Robot_Assembly.SAR2_20_b.Edge129,Robot_Assembly.SAR2_20_b.Edge129]
FEATURE [App::FeaturePython] Joint047  label="Fixed040"  # Assembly joint (typed FeaturePython)
  Activated = true
  AngleMax = 0
  AngleMin = 0
  Detach1 = false
  Detach2 = false
  Distance = 0
  Distance2 = 0
  EnableAngleMax = false
  EnableAngleMin = false
  EnableLengthMax = false
  EnableLengthMin = false
  JointType = 0 (Fixed)
  LengthMax = 0
  LengthMin = 0
  Placement1 = pos=(0,0,-2.55355) rot=(0,0,1;0rad)
  Placement2 = pos=(-7.4,10,100) rot=(0,1,0;1.5708rad)
  Reference1 = -> Assembly [Robot_Assembly.Link002.Edge4,Robot_Assembly.Link002.Edge4]
  Reference2 = -> Assembly [Robot_Assembly.SAR2_20_b.Edge130,Robot_Assembly.SAR2_20_b.Edge130]
FEATURE [App::FeaturePython] Joint048  label="Revolute"  # Assembly joint (typed FeaturePython)
  Activated = true
  AngleMax = 0
  AngleMin = 0
  Detach1 = false
  Detach2 = false
  Distance = 0
  Distance2 = 0
  EnableAngleMax = false
  EnableAngleMin = false
  EnableLengthMax = false
  EnableLengthMin = false
  JointType = 1 (Revolute)
  LengthMax = 0
  LengthMin = 0
  Placement1 = pos=(0,6,0) rot=(0.57735,0.57735,0.57735;4.18879rad)
  Placement2 = pos=(-1.42e-14,6.25,0) rot=(1,0,0;1.5708rad)
  Reference1 = -> <external RobotAssembly.FCStd>#Assembly [_609_0613_0007.Part__Feature002.Edge105,_609_0613_0007.Part__Feature002.Edge105]
  Reference2 = -> Assembly [Robot_Assembly.StringGuard.Edge43,Robot_Assembly.StringGuard.Edge43]
FEATURE [App::FeaturePython] Joint049  label="Fixed041"  # Assembly joint (typed FeaturePython)
  Activated = true
  AngleMax = 0
  AngleMin = 0
  Detach1 = false
  Detach2 = false
  Distance = 0
  Distance2 = 0
  EnableAngleMax = false
  EnableAngleMin = false
  EnableLengthMax = false
  EnableLengthMin = false
  JointType = 0 (Fixed)
  LengthMax = 0
  LengthMin = 0
  Offset2 = pos=(0,0,0) rot=(0,0,1;3.14159rad)
  Placement1 = pos=(-1.42e-14,-3.25,0) rot=(1,0,0;1.5708rad)
  Placement2 = pos=(65,15,144.5) rot=(1,0,0;4.71239rad)
  Reference1 = -> Assembly [Robot_Assembly.StringGuard.Edge10,Robot_Assembly.StringGuard.Edge10]
  Reference2 = -> Assembly [Robot_Assembly.Slides_Mount.Edge50,Robot_Assembly.Slides_Mount.Edge50]
FEATURE [App::FeaturePython] Joint050  label="Fixed042"  # Assembly joint (typed FeaturePython)
  Activated = true
  AngleMax = 0
  AngleMin = 0
  Detach1 = false
  Detach2 = false
  Distance = 0
  Distance2 = 0
  EnableAngleMax = false
  EnableAngleMin = false
  EnableLengthMax = false
  EnableLengthMin = false
  JointType = 0 (Fixed)
  LengthMax = 0
  LengthMin = 0
  Placement2 = pos=(-1.42e-14,9.25,0) rot=(1,0,0;1.5708rad)
  Reference1 = -> Assembly [Robot_Assembly.Screw009.Edge26,Robot_Assembly.Screw009.Edge26]
  Reference2 = -> Assembly [Robot_Assembly.StringGuard.Edge35,Robot_Assembly.StringGuard.Edge35]
FEATURE [App::FeaturePython] Joint051  label="Fixed043"  # Assembly joint (typed FeaturePython)
  Activated = true
  AngleMax = 0
  AngleMin = 0
  Detach1 = false
  Detach2 = false
  Distance = 0
  Distance2 = 0
  EnableAngleMax = false
  EnableAngleMin = false
  EnableLengthMax = false
  EnableLengthMin = false
  JointType = 0 (Fixed)
  LengthMax = 0
  LengthMin = 0
  Placement2 = pos=(65,10,144.5) rot=(0,0.707107,0.707107;3.14159rad)
  Reference1 = -> Assembly [Robot_Assembly.Link019.Edge27,Robot_Assembly.Link019.Edge27]
  Reference2 = -> Assembly [Robot_Assembly.Slides_Mount.Edge35,Robot_Assembly.Slides_Mount.Edge35]
FEATURE [Assembly::JointGroup] Joints001
  Group = -> [Joint002,Joint003,Joint004,Joint005,Joint009,Joint012,Joint013,Joint014,Joint015,Joint016,Joint017,Joint018,Joint019,Joint020,Joint023,Joint024,Joint027,Joint028,Joint029,Joint030,Joint031,Joint032,Joint033,Joint034,Joint035,Joint036,Joint037,Joint038,Joint039,Joint040,Joint041,Joint042,Joint043,Joint044,Joint045,Joint046,Joint047,Joint048,Joint049,Joint050,Joint051]
FEATURE [Assembly::AssemblyLink] Robot_Assembly  label="Robot Assembly"
  Group = -> [Joints001,Body,am_3637_NeveRest_Orbital_20_Gearmotor_REV2,Motor_Mount_Right,Motor_Mount_Left,Link,Slides_Mount,Screw,Screw001,Screw002,Screw003,Screw004,Screw005,Screw006,Screw007,Link001,Ras_Pi_3B_179,Link002,Screw008,Link003,Nut,Body_Top,Nut001,Link004,Link005,Link007,Link008,Link009,Link010,Link011,Link013,Link012,Link014,Link015,Link016,Link017,Link018,SAR2_20_b,SAR2_20_r,_609_0613_0007,+44 more]
  LinkedObject = -> <external RobotAssembly.FCStd>#Assembly
  Origin = -> Origin002
  Rigid = false
FEATURE [Assembly::AssemblyObject] Assembly  label="Field Assembly"
  Group = -> [Joints,Robot_Assembly,Field,GroundedJoint,Joint]
  Origin = -> Origin
  Type = Assembly

RESOLVED EXTERNAL PARTS (link-assembly join: the EXTERNAL_REF files above that resolve inside this repo's crawl, each included once):
---- part Field/Field.FCStd = doc fcstd_57fa1b39773c ----
FCSTD DOCUMENT  (FreeCAD 1.1R40077 (Git))
Label: Field
License: All rights reserved
LicenseURL: https://en.wikipedia.org/wiki/All_rights_reserved
objects: Sketcher::SketchObject×3, PartDesign::Pad×2, App::Point×1, PartDesign::Pocket×1, PartDesign::Body×1, Measure::MeasureDistance×1
note: 16 computed .brp shape members not serialized (recipe doc carries the construction recipe); baked Part::Feature solids carry a one-line shape summary decoded from their .brp

FEATURE [App::Point] Origin001
  Role = Origin
FEATURE [Sketcher::SketchObject] Sketch
  ArcFitTolerance = 1e-06
  AttachmentSupport = -> [XY_Plane]
  ExternalTypes = [0]
  FullyConstrained = true
  MakeInternals = false
  MapMode = 5
  sketch-geometry (10):
    g0: LineSegment StartX=-302.5 StartY=-302.5 StartZ=0 EndX=302.5 EndY=-302.5 EndZ=0
    g1: LineSegment StartX=302.5 StartY=-302.5 StartZ=0 EndX=302.5 EndY=302.5 EndZ=0
    g2: LineSegment StartX=302.5 StartY=302.5 StartZ=0 EndX=-302.5 EndY=302.5 EndZ=0
    g3: LineSegment StartX=-302.5 StartY=302.5 StartZ=0 EndX=-302.5 EndY=-302.5 EndZ=0
    g4: GeomPoint [constr] X=-8.69e-14 Y=6.09e-14 Z=0
    g5: LineSegment [constr] StartX=-302.5 StartY=1.261e-13 StartZ=0 EndX=302.5 EndY=8.2e-14 EndZ=0
    g6: GeomPoint X=100 Y=1.092e-13 Z=0
    g7: GeomPoint X=200 Y=9.85e-14 Z=0
    g8: GeomPoint X=-100 Y=2e-16 Z=0
    g9: GeomPoint X=-200 Y=1.276e-13 Z=0
  constraints (21):
    c: Coincident(g0,g1)
    c: Coincident(g1,g2)
    c: Coincident(g2,g3)
    c: Coincident(g3,g0)
    c: Horizontal(g0)
    c: Horizontal(g2)
    c: Vertical(g1)
    c: Vertical(g3)
    c: Coincident(g4,g-1)
    c: DistanceX(g0,g0) = 605
    c: Equal(g0,g1)
    c: Symmetric(g1,g0,g4)
    c: PointOnObject(g7,g5)
    c: PointOnObject(g6,g5)
    c: Symmetric(g1,g1,g5)
    c: Symmetric(g3,g3,g5)
    c: PointOnObject(g9,g5)
    c: DistanceX(g8,g6) = 200
    c: DistanceX(g9,g-1) = 200
    c: DistanceX(g4,g7) = 200
    c: Symmetric(g6,g8,g4)
FEATURE [PartDesign::Pad] Pad
  Direction = (0,0,1)
  Length = 18
  Length2 = 10
  Profile = -> Sketch
  ReferenceAxis = -> Sketch [N_Axis]
  Refine = true
  Suppressed = false
  Type = 0
FEATURE [Sketcher::SketchObject] Sketch001
  ArcFitTolerance = 1e-06
  AttachmentSupport = -> [Pad]
  ExternalGeometry = -> [Sketch]
  ExternalTypes = [0,0,0,0]
  FullyConstrained = true
  MakeInternals = false
  MapMode = 5
  Placement = pos=(0,0,18) rot=(0,0,1;0rad)
  sketch-geometry (2):
    g0: Circle CenterX=-100 CenterY=-6.03442e-11 CenterZ=0 NormalX=0 NormalY=0 NormalZ=1 AngleXU=0 Radius=3.175
    g1: Circle CenterX=100 CenterY=-4.44e-14 CenterZ=0 NormalX=0 NormalY=0 NormalZ=1 AngleXU=0 Radius=3.175
  constraints (4):
    c: Diameter(g0) = 6.35
    c: Coincident(g1,g-5)
    c: Equal(g1,g0)
    c: Coincident(g0,g-4)
FEATURE [PartDesign::Pad] Pad001
  BaseFeature = -> Pad
  Direction = (0,0,1)
  Length = 20
  Length2 = 10
  Profile = -> Sketch001
  ReferenceAxis = -> Sketch001 [N_Axis]
  Refine = true
  Suppressed = false
  Type = 0
FEATURE [Sketcher::SketchObject] Sketch002
  ArcFitTolerance = 1e-06
  AttachmentSupport = -> [Pad001]
  ExternalGeometry = -> [Sketch]
  ExternalTypes = [0,0]
  FullyConstrained = true
  MakeInternals = false
  MapMode = 5
  Placement = pos=(0,0,18) rot=(0,0,1;0rad)
  sketch-geometry (3):
    g0: Circle CenterX=-200 CenterY=1.024e-13 CenterZ=0 NormalX=0 NormalY=0 NormalZ=1 AngleXU=0 Radius=3.175
    g1: Circle CenterX=0 CenterY=0 CenterZ=0 NormalX=0 NormalY=0 NormalZ=1 AngleXU=0 Radius=3.175
    g2: Circle CenterX=200 CenterY=0 CenterZ=0 NormalX=0 NormalY=0 NormalZ=1 AngleXU=0 Radius=3.175
  constraints (6):
    c: Diameter(g0) = 6.35
    c: Coincident(g1,g-1)
    c: Coincident(g2,g-4)
    c: Equal(g1,g2)
    c: Equal(g2,g0)
    c: Coincident(g0,g-3)
FEATURE [PartDesign::Pocket] Pocket
  BaseFeature = -> Pad001
  Direction = (0,0,-1)
  Length = 3
  Length2 = 5
  Profile = -> Sketch002
  ReferenceAxis = -> Sketch002 [N_Axis]
  Refine = true
  Suppressed = false
  Type = 0
FEATURE [PartDesign::Body] Body  label="Field"
  AllowCompound = true
  Group = -> [Sketch,Pad,Sketch001,Pad001,Sketch002,Pocket]
  Origin = -> Origin
  Tip = -> Pocket
FEATURE [Measure::MeasureDistance] Distance  label="Distance: 20.0000 mm"
  Distance = 20
  DistanceX = 0
  DistanceY = 0
  DistanceZ = 20
  Element1 = -> Body [Pocket.Edge19]
  Element2 = -> Body [Pocket.Face5]
  Position1 = (-96.825,-6.0344e-11,38)
  Position2 = (-96.825,-6.0344e-11,18)
---- part RobotAssembly.FCStd = doc fcstd_d7b4882fe5c8 (64795 chars; too large to inline — full recipe in that document) ----
